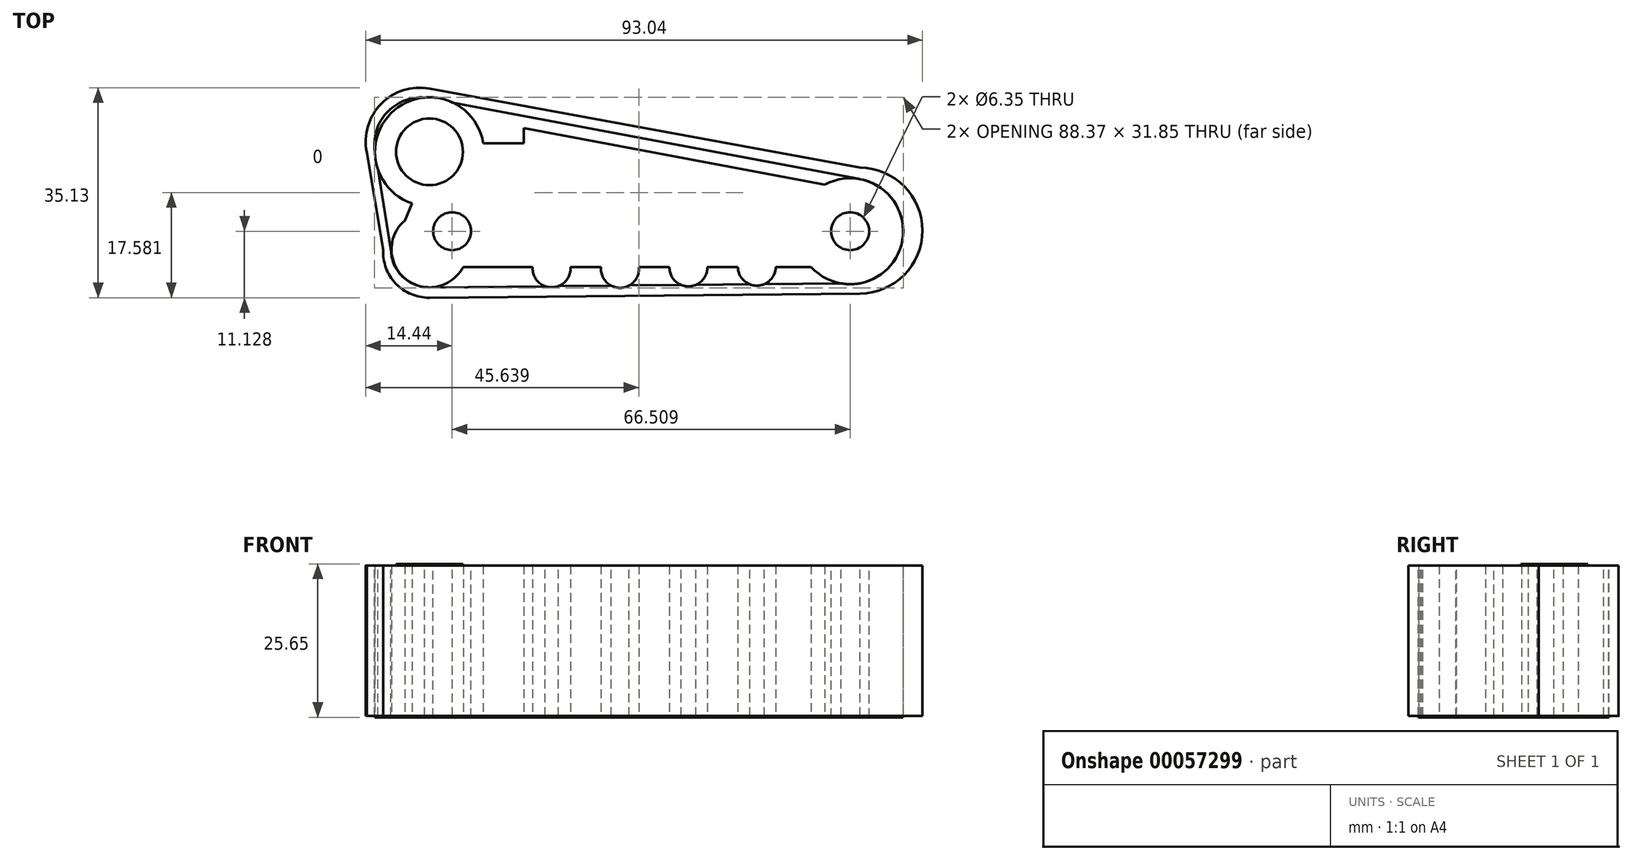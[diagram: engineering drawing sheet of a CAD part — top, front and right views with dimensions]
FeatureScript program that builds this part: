
annotation { "Feature Type Name" : "Feature", "Feature Type Description" : "" }
export const myFeature = defineFeature(function(context is Context, id is Id, definition is map)
    precondition{}
    {
        {
            var Q0;
            Q0=qCreatedBy(makeId("Top.planeOp"),FACE);
            var sketch = newSketch(context, id + "F0", { "sketchPlane" : qUnion([Q0])});
            skCircle(sketch, "E0", {"center": v(0, 0) * mm, "radius": 6.35 * mm});
            skLineSegment(sketch, "E1", {"start": v(0, -6.35) * mm, "end": v(107.92, -6.35) * mm, "construction": true});
            skLineSegment(sketch, "E2", {"start": v(107.92, -6.35) * mm, "end": v(170.9, -6.35) * mm, "construction": true});
            skLineSegment(sketch, "E3", {"start": v(-5.64, 2.92) * mm, "end": v(5.64, 2.92) * mm});
            skLineSegment(sketch, "E4", {"start": v(5.64, 2.92) * mm, "end": v(11.84, 10.65) * mm});
            skLineSegment(sketch, "E5", {"start": v(11.84, 10.65) * mm, "end": v(15.73, 15.98) * mm});
            skLineSegment(sketch, "E6", {"start": v(15.73, 15.98) * mm, "end": v(15.73, 20.3) * mm});
            skLineSegment(sketch, "E7", {"start": v(15.73, 20.3) * mm, "end": v(75.64, 9.02) * mm});
            skLineSegment(sketch, "E8", {"start": v(75.64, 9.02) * mm, "end": v(75.64, -2.92) * mm});
            skLineSegment(sketch, "E9", {"start": v(75.64, -2.92) * mm, "end": v(-5.64, -2.92) * mm});
            skLineSegment(sketch, "E10", {"start": v(-5.64, -2.92) * mm, "end": v(-5.64, 0) * mm});
            skLineSegment(sketch, "E11", {"start": v(-5.64, 0) * mm, "end": v(-5.64, 2.92) * mm});
            skArc(sketch, "E12", {"start": v(17.25, -2.92) * mm, "mid": v(20.41, -6.35) * mm, "end": v(23.58, -2.92) * mm});
            skArc(sketch, "E13", {"start": v(28.69, -2.92) * mm, "mid": v(31.84, -6.42) * mm, "end": v(35, -2.92) * mm});
            skArc(sketch, "E14", {"start": v(40.1, -2.92) * mm, "mid": v(43.27, -6.18) * mm, "end": v(46.45, -2.92) * mm});
            skArc(sketch, "E15", {"start": v(51.53, -2.92) * mm, "mid": v(54.7, -6.06) * mm, "end": v(57.88, -2.92) * mm});
            skCircle(sketch, "E16", {"center": v(0, 16.32) * mm, "radius": 9.1 * mm});
            skLineSegment(sketch, "E17", {"start": v(9, 17.77) * mm, "end": v(15.73, 17.77) * mm});
            skLineSegment(sketch, "E18", {"start": v(-2.91, 7.7) * mm, "end": v(-4.13, 4.82) * mm});
            skCircle(sketch, "E19", {"center": v(70.3, 3.05) * mm, "radius": 8.86 * mm});
            skPoint(sketch, "E19.centerSnap0", {"position": v(75.64, 3.05) * mm});
            skSolve(sketch);
        }
        {
            var Q0;
            {var subQ2=sQuery(id+"F0.wireOp",EDGE,"E10");Q0=makeQuery(id+"F0.imprint","IMPRINT",FACE,{"disambiguationData":[TD([[makeQuery(id+"F0.imprint","IMPRINT",EDGE,{"derivedFrom":subQ2}),1.0]])]});}
            var Q1;
            {var subQ0=sQuery(id+"F0.wireOp",EDGE,"E9");var subQ1=sQuery(id+"F0.wireOp",EDGE,"E0");var subQ3=makeQuery(id+"F0.imprint","INTERSECT",VERTEX,{"derivedFrom":[subQ1,subQ0]});Q1=makeQuery(id+"F0.imprint","IMPRINT",FACE,{"disambiguationData":[TD([[makeQuery(id+"F0.imprint","IMPRINT",EDGE,{"disambiguationData":[TD([[subQ3,1.0]])],"derivedFrom":subQ1}),1.0]])]});}
            var Q2;
            {var subQ0=sQuery(id+"F0.wireOp",EDGE,"E8");Q2=makeQuery(id+"F0.imprint","IMPRINT",FACE,{"disambiguationData":[TD([[makeQuery(id+"F0.imprint","IMPRINT",EDGE,{"derivedFrom":subQ0}),1.0]])]});}
            var Q3;
            {var subQ0=sQuery(id+"F0.wireOp",EDGE,"E15");Q3=makeQuery(id+"F0.imprint","IMPRINT",FACE,{"disambiguationData":[TD([[makeQuery(id+"F0.imprint","IMPRINT",EDGE,{"derivedFrom":subQ0}),1.0]])]});}
            var Q4;
            {var subQ0=sQuery(id+"F0.wireOp",EDGE,"E14");Q4=makeQuery(id+"F0.imprint","IMPRINT",FACE,{"disambiguationData":[TD([[makeQuery(id+"F0.imprint","IMPRINT",EDGE,{"derivedFrom":subQ0}),1.0]])]});}
            var Q5;
            {var subQ0=sQuery(id+"F0.wireOp",EDGE,"E13");Q5=makeQuery(id+"F0.imprint","IMPRINT",FACE,{"disambiguationData":[TD([[makeQuery(id+"F0.imprint","IMPRINT",EDGE,{"derivedFrom":subQ0}),1.0]])]});}
            var Q6;
            {var subQ0=sQuery(id+"F0.wireOp",EDGE,"E12");Q6=makeQuery(id+"F0.imprint","IMPRINT",FACE,{"disambiguationData":[TD([[makeQuery(id+"F0.imprint","IMPRINT",EDGE,{"derivedFrom":subQ0}),1.0]])]});}
            var Q7;
            {var subQ0=sQuery(id+"F0.wireOp",EDGE,"E16");var subQ1=makeQuery(id+"F0.imprint","INTERSECT",VERTEX,{"derivedFrom":[subQ0,sQuery(id+"F0.wireOp",EDGE,"E17")]});Q7=makeQuery(id+"F0.imprint","IMPRINT",FACE,{"disambiguationData":[TD([[makeQuery(id+"F0.imprint","IMPRINT",EDGE,{"disambiguationData":[TD([[subQ1,-1.0]])],"derivedFrom":subQ0}),1.0]])]});}
            var Q8;
            {var subQ0=sQuery(id+"F0.wireOp",EDGE,"E3");Q8=makeQuery(id+"F0.imprint","IMPRINT",FACE,{"disambiguationData":[TD([[makeQuery(id+"F0.imprint","IMPRINT",EDGE,{"derivedFrom":subQ0}),1.0]])]});}
            var Q9;
            {var subQ0=sQuery(id+"F0.wireOp",EDGE,"E8");Q9=makeQuery(id+"F0.imprint","IMPRINT",FACE,{"disambiguationData":[TD([[makeQuery(id+"F0.imprint","IMPRINT",EDGE,{"derivedFrom":subQ0}),-1.0]])]});}
            var Q10;
            {var subQ4=sQuery(id+"F0.wireOp",EDGE,"E3");Q10=makeQuery(id+"F0.imprint","IMPRINT",FACE,{"disambiguationData":[TD([[makeQuery(id+"F0.imprint","IMPRINT",EDGE,{"derivedFrom":subQ4}),-1.0]])]});}
            var Q11;
            {var subQ18=sQuery(id+"F0.wireOp",EDGE,"E4");Q11=makeQuery(id+"F0.imprint","IMPRINT",FACE,{"disambiguationData":[TD([[makeQuery(id+"F0.imprint","IMPRINT",EDGE,{"derivedFrom":subQ18}),-1.0]])]});}
            var Q12;
            {var subQ3=sQuery(id+"F0.wireOp",EDGE,"E4");Q12=makeQuery(id+"F0.imprint","IMPRINT",FACE,{"disambiguationData":[TD([[makeQuery(id+"F0.imprint","IMPRINT",EDGE,{"derivedFrom":subQ3}),1.0]])]});}
            extrude(context, id + "F1", {"entities" : qUnion([Q0, Q1, Q2, Q3, Q4, Q5, Q6, Q7, Q8, Q9, Q10, Q11, Q12]), "depth" : 25.4 * mm});
        }
        {
            var Q0;
            Q0=makeQuery(id+"F1.opExtrude","CAP_FACE",FACE,{"disambiguationData":[OSD([sQuery(id+"F0.wireOp",EDGE,"E0"),sQuery(id+"F0.wireOp",EDGE,"E6"),sQuery(id+"F0.wireOp",EDGE,"E7"),sQuery(id+"F0.wireOp",EDGE,"E9"),sQuery(id+"F0.wireOp",EDGE,"E12"),sQuery(id+"F0.wireOp",EDGE,"E13"),sQuery(id+"F0.wireOp",EDGE,"E14"),sQuery(id+"F0.wireOp",EDGE,"E15"),sQuery(id+"F0.wireOp",EDGE,"E16"),sQuery(id+"F0.wireOp",EDGE,"E17"),sQuery(id+"F0.wireOp",EDGE,"E18"),sQuery(id+"F0.wireOp",EDGE,"E19")])],"isStart":false});
            var sketch = newSketch(context, id + "F2", { "sketchPlane" : qUnion([Q0])});
            skLineSegment(sketch, "E20", {"start": v(71.96, 11.75) * mm, "end": v(0, 25.3) * mm});
            skLineSegment(sketch, "E21", {"start": v(71.96, -5.65) * mm, "end": v(0, -6.35) * mm});
            skLineSegment(sketch, "E22", {"start": v(-9.1, 16.25) * mm, "end": v(-6.44, 0) * mm});
            skArc(sketch, "E23", {"start": v(0, 25.3) * mm, "mid": v(-6.89, 23.12) * mm, "end": v(-9.1, 16.25) * mm});
            skArc(sketch, "E24", {"start": v(-6.44, 0) * mm, "mid": v(-4.54, -4.51) * mm, "end": v(0, -6.35) * mm});
            skLineSegment(sketch, "E25", {"start": v(0, 26.9) * mm, "end": v(71.96, 13.68) * mm});
            skLineSegment(sketch, "E26", {"start": v(71.96, -7.38) * mm, "end": v(0, -8.08) * mm});
            skLineSegment(sketch, "E27", {"start": v(-7.74, 0) * mm, "end": v(-10.47, 16.25) * mm});
            skArc(sketch, "E28", {"start": v(0, 26.9) * mm, "mid": v(-8.06, 24.35) * mm, "end": v(-10.47, 16.25) * mm});
            skArc(sketch, "E29", {"start": v(-7.74, 0) * mm, "mid": v(-5.62, -5.71) * mm, "end": v(0, -8.08) * mm});
            skArc(sketch, "E30", {"start": v(71.96, -5.65) * mm, "mid": v(79.18, 3.05) * mm, "end": v(71.96, 11.75) * mm});
            skArc(sketch, "E31", {"start": v(71.96, -7.38) * mm, "mid": v(82.39, 3.15) * mm, "end": v(71.96, 13.68) * mm});
            skSolve(sketch);
        }
        {
            var Q0;
            {var subQ22=sQuery(id+"F2.wireOp",EDGE,"E24");Q0=makeQuery(id+"F2.imprint","IMPRINT",FACE,{"disambiguationData":[TD([[makeQuery(id+"F2.imprint","IMPRINT",EDGE,{"derivedFrom":subQ22}),-1.0]])]});}
            extrude(context, id + "F3", {"entities" : qUnion([Q0]), "oppositeDirection" : true, "depth" : 25.2 * mm});
        }
        {
            var Q0;
            Q0=makeQuery(id+"F1.opExtrude","CAP_FACE",FACE,{"disambiguationData":[OSD([sQuery(id+"F0.wireOp",EDGE,"E0"),sQuery(id+"F0.wireOp",EDGE,"E6"),sQuery(id+"F0.wireOp",EDGE,"E7"),sQuery(id+"F0.wireOp",EDGE,"E9"),sQuery(id+"F0.wireOp",EDGE,"E12"),sQuery(id+"F0.wireOp",EDGE,"E13"),sQuery(id+"F0.wireOp",EDGE,"E14"),sQuery(id+"F0.wireOp",EDGE,"E15"),sQuery(id+"F0.wireOp",EDGE,"E16"),sQuery(id+"F0.wireOp",EDGE,"E17"),sQuery(id+"F0.wireOp",EDGE,"E18"),sQuery(id+"F0.wireOp",EDGE,"E19")])],"isStart":false});
            var sketch = newSketch(context, id + "F4", { "sketchPlane" : qUnion([Q0])});
            skCircle(sketch, "E32", {"center": v(0, 16.32) * mm, "radius": 5.58 * mm});
            skSolve(sketch);
        }
        {
            var Q0;
            Q0=makeQuery(id+"F4.imprint","IMPRINT",FACE,{"disambiguationData":[TD([[makeQuery(id+"F4.imprint","IMPRINT",EDGE,{"derivedFrom":sQuery(id+"F4.wireOp",EDGE,"E32")}),1.0]])]});
            extrude(context, id + "F5", {"entities" : qUnion([Q0]), "operationType" : NewBodyOperationType.ADD, "depth" : 0.25 * mm});
        }
        {
            var Q0;
            Q0=makeQuery(id+"F1.opExtrude","CAP_FACE",FACE,{"disambiguationData":[OSD([sQuery(id+"F0.wireOp",EDGE,"E0"),sQuery(id+"F0.wireOp",EDGE,"E6"),sQuery(id+"F0.wireOp",EDGE,"E7"),sQuery(id+"F0.wireOp",EDGE,"E9"),sQuery(id+"F0.wireOp",EDGE,"E12"),sQuery(id+"F0.wireOp",EDGE,"E13"),sQuery(id+"F0.wireOp",EDGE,"E14"),sQuery(id+"F0.wireOp",EDGE,"E15"),sQuery(id+"F0.wireOp",EDGE,"E16"),sQuery(id+"F0.wireOp",EDGE,"E17"),sQuery(id+"F0.wireOp",EDGE,"E18"),sQuery(id+"F0.wireOp",EDGE,"E19")])],"isStart":false});
            var sketch = newSketch(context, id + "F6", { "sketchPlane" : qUnion([Q0])});
            skCircle(sketch, "E33", {"center": v(70.3, 3.05) * mm, "radius": 3.18 * mm});
            skSolve(sketch);
        }
        {
            var Q0;
            Q0 = qSketchRegion(id + "F6", true);
            extrude(context, id + "F7", {"entities" : qUnion([Q0]), "operationType" : NewBodyOperationType.REMOVE, "oppositeDirection" : true, "depth" : 44.4 * mm});
        }
        {
            var Q0;
            Q0=makeQuery(id+"F1.opExtrude","CAP_FACE",FACE,{"disambiguationData":[OSD([sQuery(id+"F0.wireOp",EDGE,"E0"),sQuery(id+"F0.wireOp",EDGE,"E6"),sQuery(id+"F0.wireOp",EDGE,"E7"),sQuery(id+"F0.wireOp",EDGE,"E9"),sQuery(id+"F0.wireOp",EDGE,"E12"),sQuery(id+"F0.wireOp",EDGE,"E13"),sQuery(id+"F0.wireOp",EDGE,"E14"),sQuery(id+"F0.wireOp",EDGE,"E15"),sQuery(id+"F0.wireOp",EDGE,"E16"),sQuery(id+"F0.wireOp",EDGE,"E17"),sQuery(id+"F0.wireOp",EDGE,"E18"),sQuery(id+"F0.wireOp",EDGE,"E19")])],"isStart":false});
            var sketch = newSketch(context, id + "F8", { "sketchPlane" : qUnion([Q0])});
            skLineSegment(sketch, "E34", {"start": v(79.04, 1.59) * mm, "end": v(-23.03, 1.59) * mm, "construction": true});
            skPoint(sketch, "E34.endSnap0", {"position": v(79.04, 1.59) * mm});
            skLineSegment(sketch, "E35", {"start": v(70.3, 3.05) * mm, "end": v(0, 3.05) * mm, "construction": true});
            skCircle(sketch, "E36", {"center": v(3.8, 3.05) * mm, "radius": 3.18 * mm});
            skSolve(sketch);
        }
        {
            var Q0;
            Q0 = qSketchRegion(id + "F8", true);
            extrude(context, id + "F9", {"entities" : qUnion([Q0]), "operationType" : NewBodyOperationType.REMOVE, "oppositeDirection" : true, "depth" : 31.86 * mm});
        }
    });
